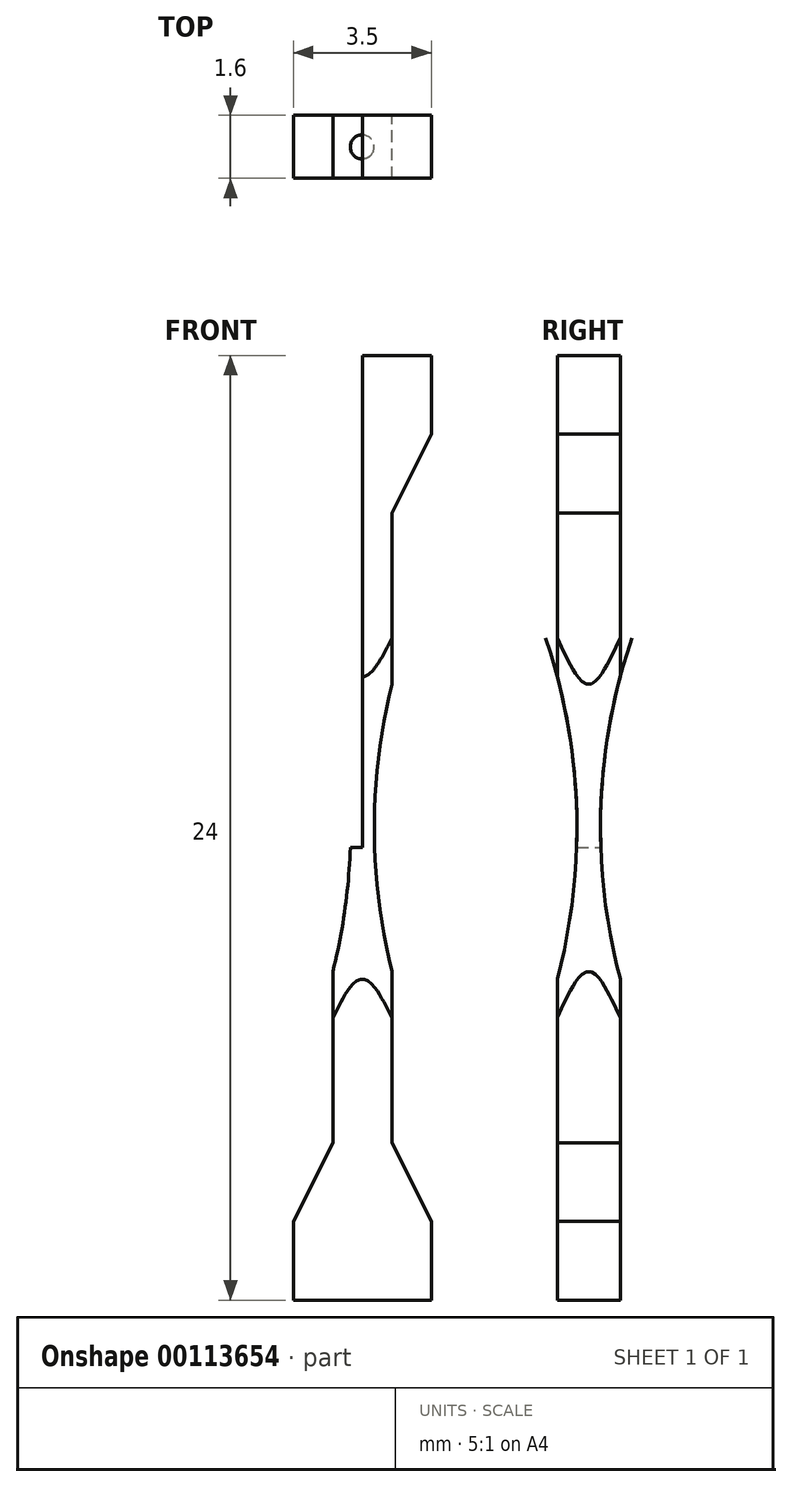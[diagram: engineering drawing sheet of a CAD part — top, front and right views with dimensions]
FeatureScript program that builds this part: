
annotation { "Feature Type Name" : "Feature", "Feature Type Description" : "" }
export const myFeature = defineFeature(function(context is Context, id is Id, definition is map)
    precondition{}
    {
        {
            var Q0;
            Q0=qCreatedBy(makeId("Front.planeOp"),FACE);
            var sketch = newSketch(context, id + "F0", { "sketchPlane" : qUnion([Q0])});
            skPoint(sketch, "E0", {"position": v(15.3, 0) * mm});
            skPoint(sketch, "E1", {"position": v(0.3, 0) * mm});
            skArc(sketch, "E2", {"start": v(0.3, 0) * mm, "mid": v(4.7, 10.6) * mm, "end": v(15.3, 15) * mm, "construction": true});
            skLineSegment(sketch, "E3", {"start": v(0, 12) * mm, "end": v(0, 0) * mm});
            skLineSegment(sketch, "E4", {"start": v(0, 0) * mm, "end": v(0.3, 0) * mm});
            skLineSegment(sketch, "E5", {"start": v(-0.33, 0.5) * mm, "end": v(0, 0.5) * mm, "construction": true});
            skPoint(sketch, "E6", {"position": v(0, 0.5) * mm});
            skArc(sketch, "E7", {"start": v(0.3, 0) * mm, "mid": v(0.3, 0.25) * mm, "end": v(0.3, 0.5) * mm});
            skArc(sketch, "E8", {"start": v(0.3, 0.5) * mm, "mid": v(4.87, 10.78) * mm, "end": v(15.3, 15) * mm});
            skLineSegment(sketch, "E9", {"start": v(0, 0.5) * mm, "end": v(0.3, 0.5) * mm, "construction": true});
            skLineSegment(sketch, "E10", {"start": v(0, 0.5) * mm, "end": v(0.3, 0.5) * mm});
            skLineSegment(sketch, "E11", {"start": v(0, 12) * mm, "end": v(6.3, 12) * mm});
            skSolve(sketch);
        }
        {
            var Q0;
            {var subQ2=sQuery(id+"F0.wireOp",EDGE,"E10");Q0=makeQuery(id+"F0.imprint","IMPRINT",FACE,{"disambiguationData":[TD([[makeQuery(id+"F0.imprint","IMPRINT",EDGE,{"derivedFrom":subQ2}),1.0]])]});}
            var Q1;
            Q1=sQuery(id+"F0.wireOp",EDGE,"E3");
            revolve(context, id + "F1", {"entities" : qUnion([Q0]), "axis" : qUnion([Q1]), "revolveType" : RevolveType.FULL});
        }
        {
            var Q0;
            {var subQ0=sQuery(id+"F0.wireOp",EDGE,"E4");Q0=makeQuery(id+"F0.imprint","IMPRINT",FACE,{"disambiguationData":[TD([[makeQuery(id+"F0.imprint","IMPRINT",EDGE,{"derivedFrom":subQ0}),1.0]])]});}
            var Q1;
            Q1=sQuery(id+"F0.wireOp",EDGE,"E3");
            revolve(context, id + "F2", {"entities" : qUnion([Q0]), "axis" : qUnion([Q1]), "revolveType" : RevolveType.FULL});
        }
        {
            var Q0;
            Q0=qCreatedBy(makeId("Front.planeOp"),FACE);
            var sketch = newSketch(context, id + "F3", { "sketchPlane" : qUnion([Q0])});
            skLineSegment(sketch, "E12", {"start": v(0.75, 0) * mm, "end": v(0.75, 8) * mm});
            skLineSegment(sketch, "E13", {"start": v(0.75, 8) * mm, "end": v(1.75, 10) * mm});
            skLineSegment(sketch, "E14", {"start": v(1.75, 10) * mm, "end": v(1.75, 12) * mm});
            skLineSegment(sketch, "E15", {"start": v(1.75, 12) * mm, "end": v(0, 12) * mm});
            skLineSegment(sketch, "E16", {"start": v(0, 12) * mm, "end": v(0, 0) * mm});
            skLineSegment(sketch, "E17", {"start": v(0, 0) * mm, "end": v(0.75, 0) * mm});
            skSolve(sketch);
        }
        {
            var Q0;
            Q0=makeQuery(id+"F3.imprint","IMPRINT",FACE,{"disambiguationData":[TD([[makeQuery(id+"F3.imprint","IMPRINT",EDGE,{"derivedFrom":sQuery(id+"F3.wireOp",EDGE,"p0L3ZjBc-SygR-bWeM-3u15-98zRel55rwWZ.bottom")}),-1.0]])]});
            var Q1;
            Q1=makeQuery(id+"F3.imprint","IMPRINT",FACE,{"disambiguationData":[TD([[makeQuery(id+"F3.imprint","IMPRINT",EDGE,{"derivedFrom":sQuery(id+"F3.wireOp",EDGE,"E12")}),1.0]])]});
            extrude(context, id + "F4", {"entities" : qUnion([Q0, Q1]), "operationType" : NewBodyOperationType.INTERSECT, "depth" : 1.6 * mm, "symmetric" : true});
        }
        {
            var Q0;
            Q0=makeQuery(id+"F1.opRevolve","SWEPT_BODY",BODY,{"disambiguationData":[OSD([sQuery(id+"F0.wireOp",EDGE,"OcnPvCSy-cZS5-JDQh-wchw-9l9LrSL49Ts8"),sQuery(id+"F0.wireOp",EDGE,"Dct7jnFl-Wa0s-DOEL-NKnk-l80QN2pxv5ud"),sQuery(id+"F0.wireOp",EDGE,"dMe9K8Vx-obDh-k0uA-Upyp-ExFzSnsmPXVj"),sQuery(id+"F0.wireOp",EDGE,"ASEVp0sq-exOI-wicY-23Um-DL8Uq5OcPyFh"),sQuery(id+"F0.wireOp",EDGE,"b3V7QA5D-BfOZ-9Ogp-569r-IGBEo0v84lE0"),sQuery(id+"F0.wireOp",EDGE,"E3"),sQuery(id+"F0.wireOp",EDGE,"E4")])]});
            var Q1;
            Q1=qCreatedBy(makeId("Top.planeOp"),FACE);
            mirror(context, id + "F5", {"operationType" : NewBodyOperationType.ADD, "entities" : qUnion([Q0]), "mirrorPlane" : qUnion([Q1])});
        }
        {
            var Q0;
            Q0=makeQuery(id+"F1.opRevolve","SWEPT_BODY",BODY,{"disambiguationData":[OSD([sQuery(id+"F0.wireOp",EDGE,"b3V7QA5D-BfOZ-9Ogp-569r-IGBEo0v84lE0"),sQuery(id+"F0.wireOp",EDGE,"E3"),sQuery(id+"F0.wireOp",EDGE,"E4"),sQuery(id+"F0.wireOp",EDGE,"tU3sDNKk-SkTn-PNZ5-DSya-0HxhoEAgS3CD")])]});
            var Q1;
            Q1=makeQuery(id+"F5.opPattern","COPY",BODY,{"derivedFrom":makeQuery(id+"F1.opRevolve","SWEPT_BODY",BODY,{"disambiguationData":[OSD([sQuery(id+"F0.wireOp",EDGE,"E3"),sQuery(id+"F0.wireOp",EDGE,"E8"),sQuery(id+"F0.wireOp",EDGE,"E10"),sQuery(id+"F0.wireOp",EDGE,"E11")])]}),"instanceName":"1"});
            var Q2;
            Q2=qCreatedBy(makeId("Right.planeOp"),FACE);
            mirror(context, id + "F6", {"operationType" : NewBodyOperationType.ADD, "entities" : qUnion([Q0, Q1]), "mirrorPlane" : qUnion([Q2])});
        }
        {
            var Q0;
            Q0=makeQuery(id+"F2.opRevolve","SWEPT_BODY",BODY,{"disambiguationData":[OSD([sQuery(id+"F0.wireOp",EDGE,"E3"),sQuery(id+"F0.wireOp",EDGE,"E4"),sQuery(id+"F0.wireOp",EDGE,"E7"),sQuery(id+"F0.wireOp",EDGE,"E10")])]});
            var Q1;
            Q1=qCreatedBy(makeId("Top.planeOp"),FACE);
            mirror(context, id + "F7", {"operationType" : NewBodyOperationType.ADD, "entities" : qUnion([Q0]), "mirrorPlane" : qUnion([Q1])});
        }
    });
